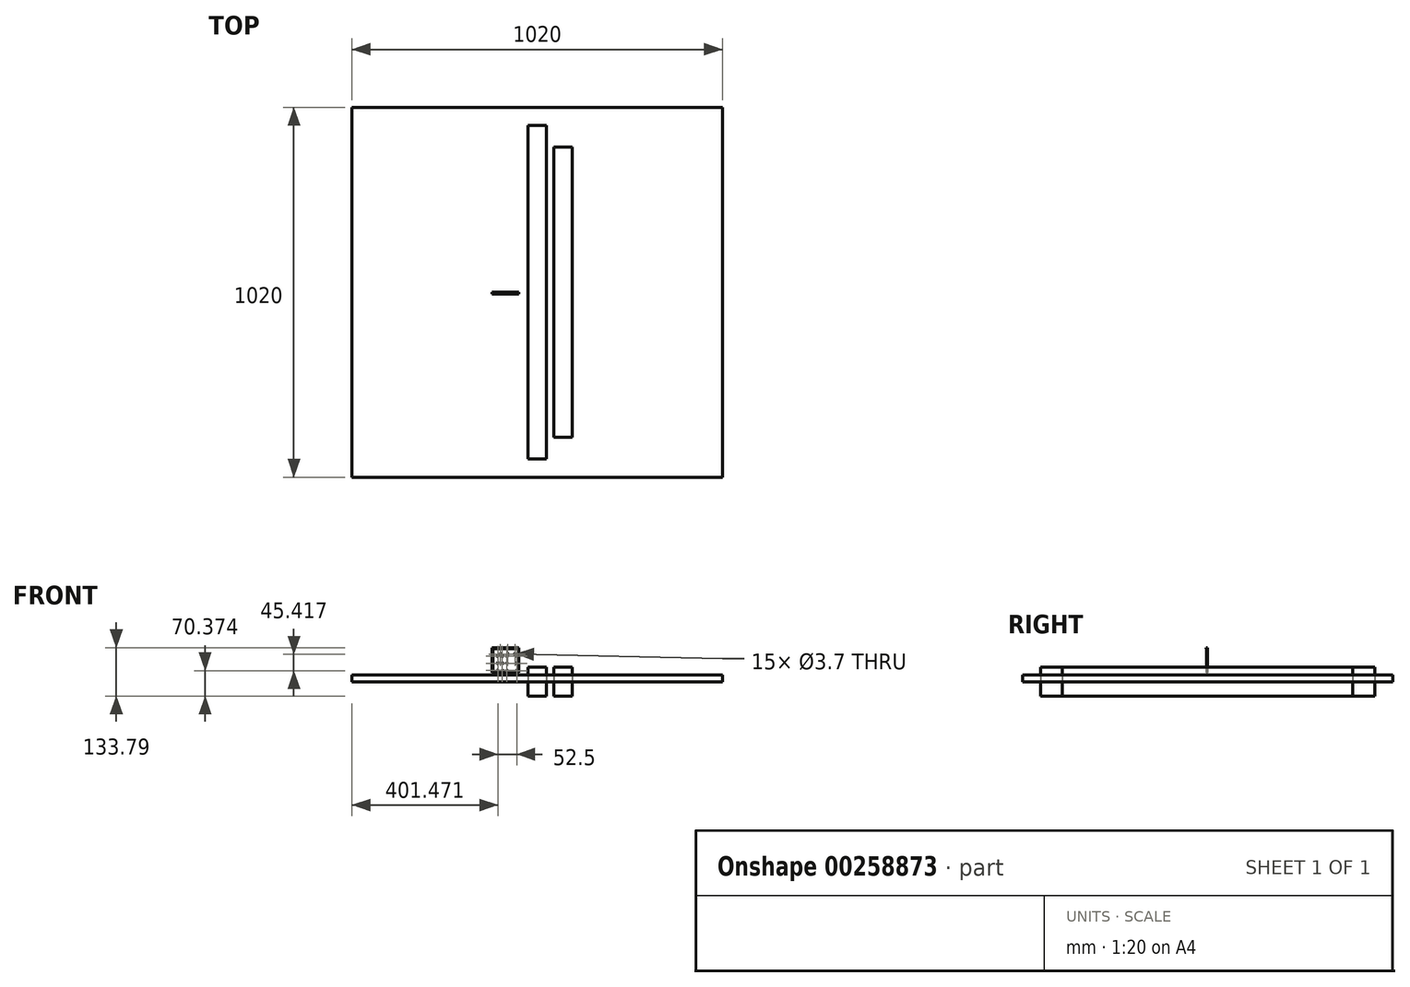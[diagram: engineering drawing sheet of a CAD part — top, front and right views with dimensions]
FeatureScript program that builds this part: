
annotation { "Feature Type Name" : "Feature", "Feature Type Description" : "" }
export const myFeature = defineFeature(function(context is Context, id is Id, definition is map)
    precondition{}
    {
        {
            var Q0;
            Q0=qCreatedBy(makeId("Front.planeOp"),FACE);
            var sketch = newSketch(context, id + "F0", { "sketchPlane" : qUnion([Q0])});
            skLineSegment(sketch, "E0.bottom", {"start": v(-25, 40) * mm, "end": v(25, 40) * mm});
            skLineSegment(sketch, "E0.top", {"start": v(-25, -40) * mm, "end": v(25, -40) * mm});
            skLineSegment(sketch, "E0.left", {"start": v(-25, 40) * mm, "end": v(-25, -40) * mm});
            skLineSegment(sketch, "E0.right", {"start": v(25, 40) * mm, "end": v(25, -40) * mm});
            skPoint(sketch, "E0.middle", {"position": v(0, 0) * mm});
            skLineSegment(sketch, "E1.bottom", {"start": v(46, 40) * mm, "end": v(96, 40) * mm});
            skLineSegment(sketch, "E1.top", {"start": v(46, -40) * mm, "end": v(96, -40) * mm});
            skLineSegment(sketch, "E1.left", {"start": v(46, 40) * mm, "end": v(46, -40) * mm});
            skLineSegment(sketch, "E1.right", {"start": v(96, 40) * mm, "end": v(96, -40) * mm});
            skPoint(sketch, "E1.middle", {"position": v(71, 0) * mm});
            skSolve(sketch);
        }
        {
            var Q0;
            Q0=makeQuery(id+"F0.imprint","IMPRINT",FACE,{"disambiguationData":[TD([[makeQuery(id+"F0.imprint","IMPRINT",EDGE,{"derivedFrom":sQuery(id+"F0.wireOp",EDGE,"E0.bottom")}),-1.0]])]});
            extrude(context, id + "F1", {"entities" : qUnion([Q0]), "endBound" : BoundingType.SYMMETRIC, "depth" : 920 * mm});
        }
        {
            var Q0;
            Q0=makeQuery(id+"F0.imprint","IMPRINT",FACE,{"disambiguationData":[TD([[makeQuery(id+"F0.imprint","IMPRINT",EDGE,{"derivedFrom":sQuery(id+"F0.wireOp",EDGE,"E1.bottom")}),-1.0]])]});
            extrude(context, id + "F2", {"entities" : qUnion([Q0]), "endBound" : BoundingType.SYMMETRIC, "depth" : 800 * mm});
        }
        {
            var Q0;
            Q0=qCreatedBy(makeId("Front.planeOp"),FACE);
            var sketch = newSketch(context, id + "F3", { "sketchPlane" : qUnion([Q0])});
            skLineSegment(sketch, "E2.bottom", {"start": v(-121.03, 10.8) * mm, "end": v(-71.03, 10.8) * mm, "construction": true});
            skLineSegment(sketch, "E2.top", {"start": v(-121.03, 90.8) * mm, "end": v(-71.03, 90.8) * mm, "construction": true});
            skLineSegment(sketch, "E2.left", {"start": v(-121.03, 10.8) * mm, "end": v(-121.03, 90.8) * mm, "construction": true});
            skLineSegment(sketch, "E2.right", {"start": v(-71.03, 10.8) * mm, "end": v(-71.03, 90.8) * mm, "construction": true});
            skPoint(sketch, "E2.middle", {"position": v(-96.03, 50.8) * mm});
            skLineSegment(sketch, "E3", {"start": v(-96.03, 98.2) * mm, "end": v(-96.03, 0) * mm, "construction": true});
            skLineSegment(sketch, "E4", {"start": v(-125.82, 50.8) * mm, "end": v(-25.01, 50.8) * mm, "construction": true});
            skPoint(sketch, "E4.endSnap0", {"position": v(-71.03, 50.8) * mm});
            skLineSegment(sketch, "E5", {"start": v(-136.5, 70.8) * mm, "end": v(-28.05, 70.8) * mm, "construction": true});
            skLineSegment(sketch, "E6", {"start": v(-133.04, 30.8) * mm, "end": v(-27.51, 30.8) * mm, "construction": true});
            skLineSegment(sketch, "E7", {"start": v(-108.53, 97.75) * mm, "end": v(-108.53, 2.14) * mm, "construction": true});
            skLineSegment(sketch, "E8", {"start": v(-83.53, 101.58) * mm, "end": v(-83.53, 0) * mm, "construction": true});
            skLineSegment(sketch, "E9.bottom", {"start": v(-71.03, 10.8) * mm, "end": v(-121.03, 10.8) * mm});
            skLineSegment(sketch, "E9.top", {"start": v(-71.03, 90.8) * mm, "end": v(-121.03, 90.8) * mm, "construction": true});
            skLineSegment(sketch, "E9.left", {"start": v(-71.03, 10.8) * mm, "end": v(-71.03, 90.8) * mm});
            skLineSegment(sketch, "E10.bottom", {"start": v(-71.03, 10.8) * mm, "end": v(-124.03, 10.8) * mm});
            skLineSegment(sketch, "E10.top", {"start": v(-43.03, 93.8) * mm, "end": v(-124.03, 93.8) * mm});
            skLineSegment(sketch, "E10.left", {"start": v(-71.03, 10.8) * mm, "end": v(-71.03, 93.8) * mm});
            skLineSegment(sketch, "E10.right", {"start": v(-124.03, 25.14) * mm, "end": v(-124.03, 93.8) * mm});
            skLineSegment(sketch, "E11.0", {"start": v(-124.03, 91.04) * mm, "end": v(-43.03, 91.04) * mm});
            skLineSegment(sketch, "E11.1", {"start": v(-121.28, 8.45) * mm, "end": v(-121.28, 10.8) * mm});
            skCircle(sketch, "E12", {"center": v(-108.53, 70.8) * mm, "radius": 1.85 * mm});
            skCircle(sketch, "E13", {"center": v(-96.03, 70.8) * mm, "radius": 1.85 * mm});
            skCircle(sketch, "E14", {"center": v(-83.53, 70.8) * mm, "radius": 1.85 * mm});
            skCircle(sketch, "E15", {"center": v(-108.53, 50.8) * mm, "radius": 1.85 * mm});
            skCircle(sketch, "E16", {"center": v(-108.53, 30.8) * mm, "radius": 1.85 * mm});
            skCircle(sketch, "E17", {"center": v(-96.03, 30.8) * mm, "radius": 1.85 * mm});
            skCircle(sketch, "E18", {"center": v(-83.53, 50.8) * mm, "radius": 1.85 * mm});
            skCircle(sketch, "E19", {"center": v(-83.53, 30.8) * mm, "radius": 1.85 * mm});
            skCircle(sketch, "E20", {"center": v(-96.03, 50.8) * mm, "radius": 1.85 * mm});
            skLineSegment(sketch, "E21.bottom", {"start": v(-121.03, 90.8) * mm, "end": v(-41.03, 90.8) * mm, "construction": true});
            skLineSegment(sketch, "E21.top", {"start": v(-121.03, 10.8) * mm, "end": v(-41.03, 10.8) * mm, "construction": true});
            skLineSegment(sketch, "E21.left", {"start": v(-121.03, 90.8) * mm, "end": v(-121.03, 10.8) * mm, "construction": true});
            skLineSegment(sketch, "E21.right", {"start": v(-41.03, 90.8) * mm, "end": v(-41.03, 10.8) * mm, "construction": true});
            skLineSegment(sketch, "E22", {"start": v(-56.03, 99.27) * mm, "end": v(-56.03, 2.31) * mm, "construction": true});
            skCircle(sketch, "E23", {"center": v(-56.03, 70.8) * mm, "radius": 1.85 * mm});
            skCircle(sketch, "E24", {"center": v(-56.03, 50.8) * mm, "radius": 1.85 * mm});
            skCircle(sketch, "E25", {"center": v(-56.03, 30.37) * mm, "radius": 1.85 * mm});
            skLineSegment(sketch, "E26.MirrorCS", {"start": v(-43.03, 10.8) * mm, "end": v(-43.03, 93.8) * mm, "construction": true});
            skLineSegment(sketch, "E27.MirrorCS", {"start": v(-45.78, 8.45) * mm, "end": v(-45.78, 10.8) * mm});
            skLineSegment(sketch, "E28", {"start": v(-124.03, 25.14) * mm, "end": v(-43.03, 25.14) * mm});
            skLineSegment(sketch, "E29.trimOffspring", {"start": v(-121.28, 25.14) * mm, "end": v(-121.28, 91.04) * mm});
            skLineSegment(sketch, "E30.trimOffspring", {"start": v(-45.78, 25.14) * mm, "end": v(-45.78, 91.04) * mm, "construction": true});
            skLineSegment(sketch, "E31", {"start": v(-111.03, 84.6) * mm, "end": v(-111.03, 77) * mm, "construction": true});
            skLineSegment(sketch, "E32", {"start": v(-111.03, 64.6) * mm, "end": v(-111.03, 57) * mm, "construction": true});
            skLineSegment(sketch, "E33", {"start": v(-111.03, 44.6) * mm, "end": v(-111.03, 37) * mm, "construction": true});
            skLineSegment(sketch, "E34", {"start": v(-111.03, 64.6) * mm, "end": v(-111.03, 70.8) * mm, "construction": true});
            skLineSegment(sketch, "E35", {"start": v(-111.03, 70.8) * mm, "end": v(-111.03, 77) * mm, "construction": true});
            skLineSegment(sketch, "E36", {"start": v(-111.03, 57) * mm, "end": v(-111.03, 50.8) * mm, "construction": true});
            skLineSegment(sketch, "E37", {"start": v(-111.03, 50.8) * mm, "end": v(-111.03, 44.6) * mm, "construction": true});
            skLineSegment(sketch, "E38", {"start": v(-111.03, 37) * mm, "end": v(-111.03, 30.8) * mm, "construction": true});
            skLineSegment(sketch, "E39", {"start": v(-111.03, 84.6) * mm, "end": v(-111.03, 90.8) * mm, "construction": true});
            skArc(sketch, "E40.0.startCap", {"start": v(-111.53, 84.6) * mm, "mid": v(-111.03, 85.1) * mm, "end": v(-110.53, 84.6) * mm, "construction": true});
            skArc(sketch, "E40.0.endCap", {"start": v(-110.53, 77) * mm, "mid": v(-111.03, 76.5) * mm, "end": v(-111.53, 77) * mm, "construction": true});
            skLineSegment(sketch, "E40.0.left", {"start": v(-110.53, 84.6) * mm, "end": v(-110.53, 77) * mm, "construction": true});
            skLineSegment(sketch, "E40.0.right", {"start": v(-111.53, 84.6) * mm, "end": v(-111.53, 77) * mm, "construction": true});
            skArc(sketch, "E40.1.startCap", {"start": v(-111.53, 64.6) * mm, "mid": v(-111.03, 65.1) * mm, "end": v(-110.53, 64.6) * mm, "construction": true});
            skArc(sketch, "E40.1.endCap", {"start": v(-110.53, 57) * mm, "mid": v(-111.03, 56.5) * mm, "end": v(-111.53, 57) * mm, "construction": true});
            skLineSegment(sketch, "E40.1.left", {"start": v(-110.53, 64.6) * mm, "end": v(-110.53, 57) * mm, "construction": true});
            skLineSegment(sketch, "E40.1.right", {"start": v(-111.53, 64.6) * mm, "end": v(-111.53, 57) * mm, "construction": true});
            skArc(sketch, "E40.2.startCap", {"start": v(-111.53, 44.6) * mm, "mid": v(-111.03, 45.1) * mm, "end": v(-110.53, 44.6) * mm, "construction": true});
            skArc(sketch, "E40.2.endCap", {"start": v(-110.53, 37) * mm, "mid": v(-111.03, 36.5) * mm, "end": v(-111.53, 37) * mm});
            skLineSegment(sketch, "E40.2.left", {"start": v(-110.53, 44.6) * mm, "end": v(-110.53, 37) * mm, "construction": true});
            skLineSegment(sketch, "E40.2.right", {"start": v(-111.53, 44.6) * mm, "end": v(-111.53, 37) * mm, "construction": true});
            skLineSegment(sketch, "E41", {"start": v(-50.98, 93.8) * mm, "end": v(-50.98, 25.14) * mm});
            skLineSegment(sketch, "E42", {"start": v(-115.39, 75.8) * mm, "end": v(-36.17, 75.8) * mm, "construction": true});
            skCircle(sketch, "E43", {"center": v(-101.03, 75.8) * mm, "radius": 1.85 * mm});
            skCircle(sketch, "E44.1.0.0", {"center": v(-81.03, 75.8) * mm, "radius": 1.85 * mm});
            skLineSegment(sketch, "E44.direction1", {"start": v(-101.03, 75.8) * mm, "end": v(-81.03, 75.8) * mm, "construction": true});
            skCircle(sketch, "E45.0.2.0", {"center": v(-61.03, 75.8) * mm, "radius": 1.85 * mm});
            skSolve(sketch);
        }
        {
            var Q0;
            {var subQ5=sQuery(id+"F3.wireOp",EDGE,"E29.trimOffspring");Q0=makeQuery(id+"F3.imprint","IMPRINT",FACE,{"disambiguationData":[TD([[makeQuery(id+"F3.imprint","IMPRINT",EDGE,{"derivedFrom":subQ5}),1.0]])]});}
            var Q1;
            {var subQ1=sQuery(id+"F3.wireOp",EDGE,"E10.right");var subQ4=sQuery(id+"F3.wireOp",EDGE,"E10.top");var subQ5=makeQuery(id+"F3.imprint","INTERSECT",VERTEX,{"derivedFrom":[subQ4,subQ1]});Q1=makeQuery(id+"F3.imprint","IMPRINT",FACE,{"disambiguationData":[TD([[makeQuery(id+"F3.imprint","IMPRINT",EDGE,{"disambiguationData":[TD([[subQ5,1.0]])],"derivedFrom":subQ4}),1.0]])]});}
            var Q2;
            Q2=makeQuery(id+"F3.imprint","IMPRINT",FACE,{"disambiguationData":[TD([[makeQuery(id+"F3.imprint","IMPRINT",EDGE,{"derivedFrom":sQuery(id+"F3.wireOp",EDGE,"E12")}),-1.0]])]});
            var Q3;
            {var subQ0=sQuery(id+"F3.wireOp",EDGE,"E26.MirrorCS");var subQ4=sQuery(id+"F3.wireOp",EDGE,"E10.top");var subQ5=makeQuery(id+"F3.imprint","INTERSECT",VERTEX,{"derivedFrom":[subQ4,subQ0]});Q3=makeQuery(id+"F3.imprint","IMPRINT",FACE,{"disambiguationData":[TD([[makeQuery(id+"F3.imprint","IMPRINT",EDGE,{"disambiguationData":[TD([[subQ5,-1.0]])],"derivedFrom":subQ4}),1.0]])]});}
            var Q4;
            Q4=makeQuery(id+"F3.imprint","IMPRINT",FACE,{"disambiguationData":[TD([[makeQuery(id+"F3.imprint","IMPRINT",EDGE,{"derivedFrom":sQuery(id+"F3.wireOp",EDGE,"E23")}),-1.0]])]});
            extrude(context, id + "F4", {"entities" : qUnion([Q0, Q1, Q2, Q3, Q4]), "depth" : 1.5 * mm});
        }
        {
            var Q0;
            {var subQ1=sQuery(id+"F3.wireOp",EDGE,"E10.right");var subQ4=sQuery(id+"F3.wireOp",EDGE,"E10.top");var subQ5=makeQuery(id+"F3.imprint","INTERSECT",VERTEX,{"derivedFrom":[subQ4,subQ1]});Q0=makeQuery(id+"F3.imprint","IMPRINT",FACE,{"disambiguationData":[TD([[makeQuery(id+"F3.imprint","IMPRINT",EDGE,{"disambiguationData":[TD([[subQ5,1.0]])],"derivedFrom":subQ4}),1.0]])]});}
            var Q1;
            {var subQ0=sQuery(id+"F3.wireOp",EDGE,"E10.left");var subQ1=sQuery(id+"F3.wireOp",EDGE,"E10.top");var subQ2=makeQuery(id+"F3.imprint","INTERSECT",VERTEX,{"derivedFrom":[subQ1,subQ0]});Q1=makeQuery(id+"F3.imprint","IMPRINT",FACE,{"disambiguationData":[TD([[makeQuery(id+"F3.imprint","IMPRINT",EDGE,{"disambiguationData":[TD([[subQ2,1.0]])],"derivedFrom":subQ1}),1.0]])]});}
            extrude(context, id + "F5", {"entities" : qUnion([Q0, Q1]), "operationType" : NewBodyOperationType.ADD, "depth" : 5 * mm});
        }
        {
            var Q0;
            {var subQ5=sQuery(id+"F3.wireOp",EDGE,"E29.trimOffspring");Q0=makeQuery(id+"F3.imprint","IMPRINT",FACE,{"disambiguationData":[TD([[makeQuery(id+"F3.imprint","IMPRINT",EDGE,{"derivedFrom":subQ5}),1.0]])]});}
            extrude(context, id + "F6", {"entities" : qUnion([Q0]), "operationType" : NewBodyOperationType.ADD, "depth" : 3.5 * mm});
        }
        {
            var Q0;
            Q0=qCreatedBy(makeId("Top.planeOp"),FACE);
            var sketch = newSketch(context, id + "F7", { "sketchPlane" : qUnion([Q0])});
            skLineSegment(sketch, "E46.bottom", {"start": v(-510, 510) * mm, "end": v(510, 510) * mm});
            skLineSegment(sketch, "E46.top", {"start": v(-510, -510) * mm, "end": v(510, -510) * mm});
            skLineSegment(sketch, "E46.left", {"start": v(-510, 510) * mm, "end": v(-510, -510) * mm});
            skLineSegment(sketch, "E46.right", {"start": v(510, 510) * mm, "end": v(510, -510) * mm});
            skPoint(sketch, "E46.middle", {"position": v(0, 0) * mm});
            skSolve(sketch);
        }
        {
            var Q0;
            Q0=makeQuery(id+"F7.imprint","IMPRINT",FACE,{"disambiguationData":[TD([[makeQuery(id+"F7.imprint","IMPRINT",EDGE,{"derivedFrom":sQuery(id+"F7.wireOp",EDGE,"E46.bottom")}),-1.0]])]});
            extrude(context, id + "F8", {"entities" : qUnion([Q0]), "depth" : 18 * mm});
        }
    });
